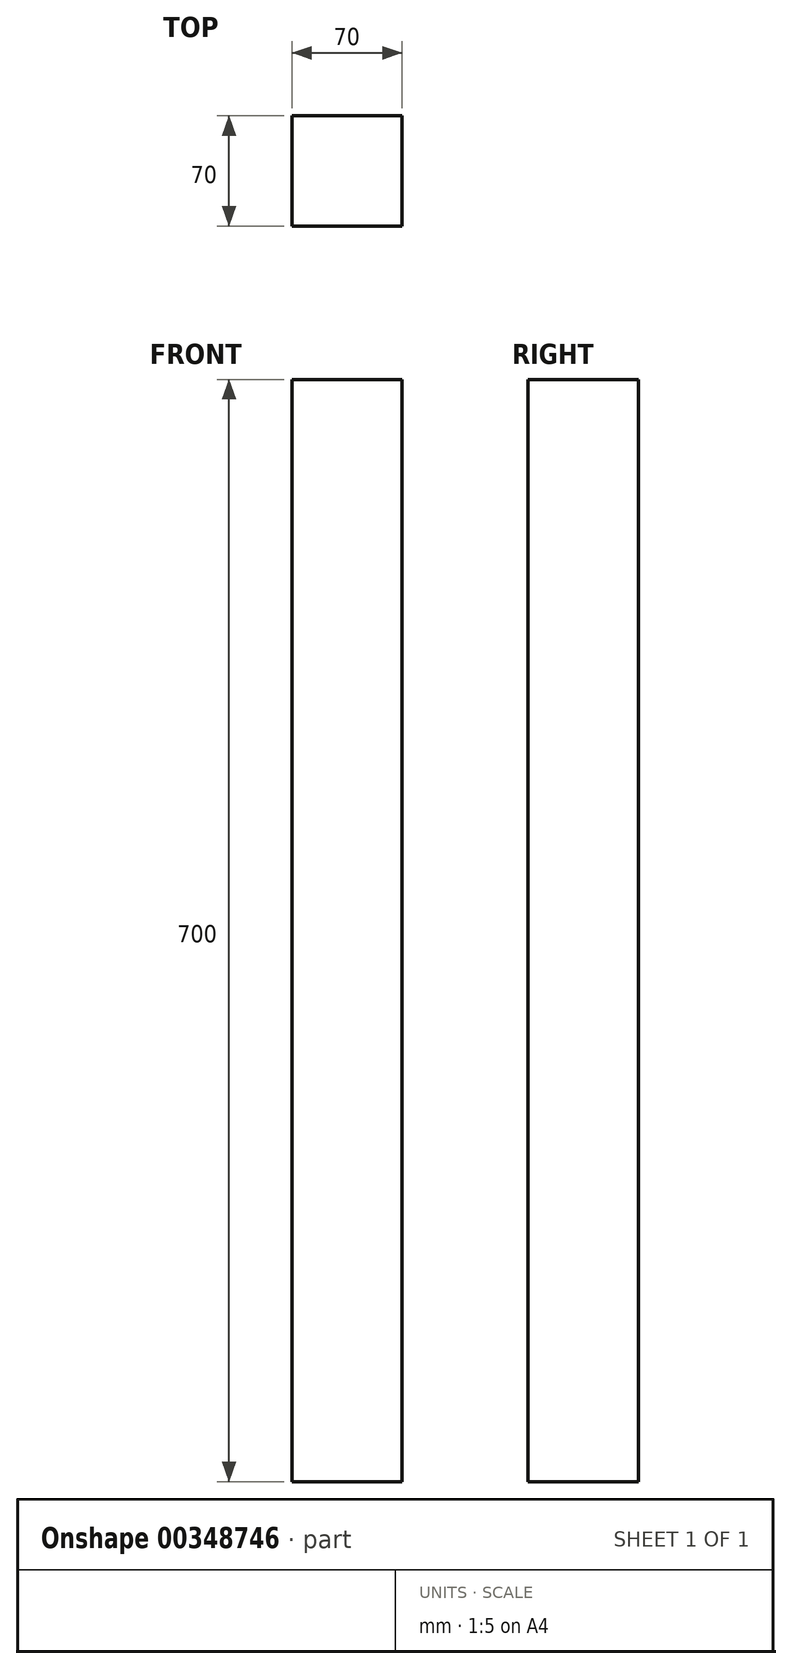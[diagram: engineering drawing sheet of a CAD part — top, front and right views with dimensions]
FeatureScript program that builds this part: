
annotation { "Feature Type Name" : "Feature", "Feature Type Description" : "" }
export const myFeature = defineFeature(function(context is Context, id is Id, definition is map)
    precondition{}
    {
        {
            var Q0;
            Q0=qCreatedBy(makeId("Top.planeOp"),FACE);
            var sketch = newSketch(context, id + "F0", { "sketchPlane" : qUnion([Q0])});
            skLineSegment(sketch, "E0.bottom", {"start": v(35, -35) * mm, "end": v(-35, -35) * mm});
            skLineSegment(sketch, "E0.top", {"start": v(35, 35) * mm, "end": v(-35, 35) * mm});
            skLineSegment(sketch, "E0.left", {"start": v(35, -35) * mm, "end": v(35, 35) * mm});
            skLineSegment(sketch, "E0.right", {"start": v(-35, -35) * mm, "end": v(-35, 35) * mm});
            skPoint(sketch, "E0.middle", {"position": v(0, 0) * mm});
            skSolve(sketch);
        }
        {
            var Q0;
            Q0 = qSketchRegion(id + "F0", true);
            extrude(context, id + "F1", {"entities" : qUnion([Q0]), "depth" : 700 * mm});
        }
    });
